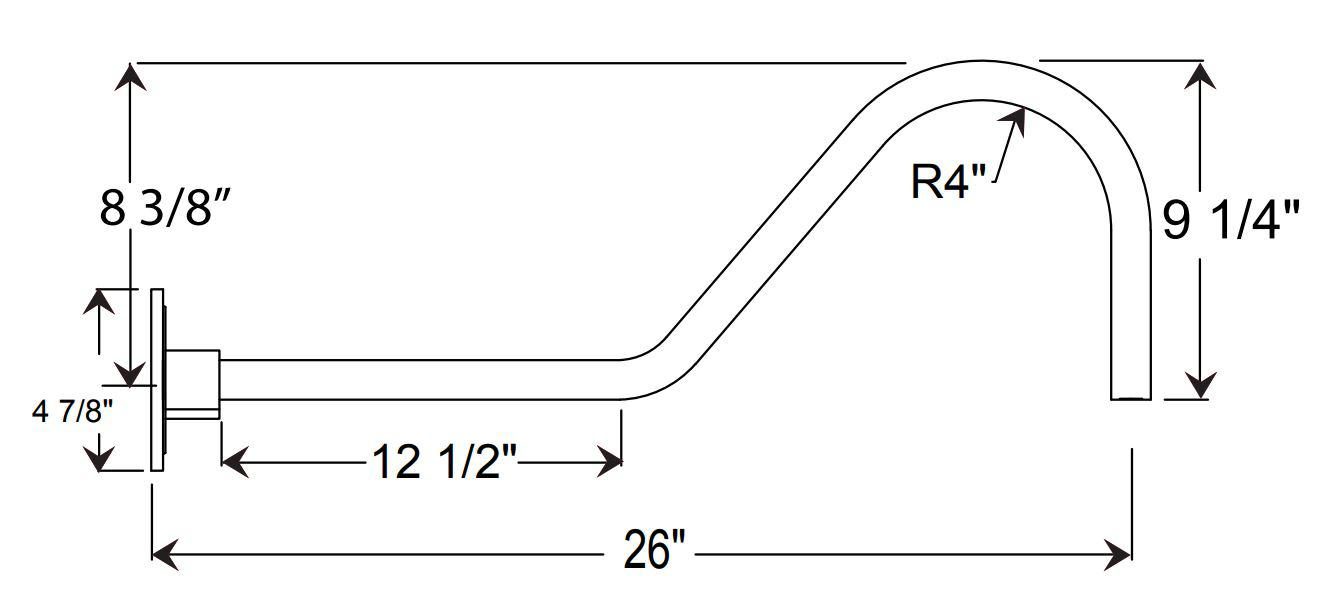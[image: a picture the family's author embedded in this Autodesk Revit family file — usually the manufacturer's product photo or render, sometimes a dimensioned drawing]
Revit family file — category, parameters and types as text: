
# Revit family: OSAC-24,36 MB
name_source: partatom
category: Lighting Fixtures
units: mm (PartAtom-declared; Revit-internal decimal feet)

## family parameters
Always vertical = Yes
Cut with Voids When Loaded = No
Light Source = Yes
OmniClass Number = 23.80.70.00
OmniClass Title = Lighting
Part Type = Normal
Room Calculation Point = No
Round Connector Dimension = Use Diameter
Shared = No
Work Plane-Based = No

## types (2) — shared parameters
Apparent Load = 200 VA
Body Colour = Spun aluminium
Body Material = body
Bulb = Bulb
CRI = >90
Color Filter = 16777215
Construction Material = Heavy Duty spun aluminum.
Default Elevation = 0' - 0"
Description = 120-277 Voltage
Dimming = 1%
Dimming Lamp Color Temperature Shift = <None>
Efficiency = 65-125 lumens per watt
INSIDE BODY = INSIDE BODY
Lamp = MB
Life = L70 50,000 hours
Load Classification = Lighting
Manufacturer = ANP Lighting
Photometric Web File = generic.ies
Power Factor = 1
Tilt Angle = 90.00°
URL = https://www.anplighting.com
Voltage = 277 V
Warranty = 5 year limited warranty
Wattage Comments = 200W Max

## per-type parameters (varying)
| type | Fixture Diameter | Fixture Height | OSAC24 | OSAC36 | Weight |
| OSAC24 | 2' - 0" | 0' - 8" | Yes | No | 6.5 lbs |
| OSAC36 | 3' - 0" | 1' - 0" | No | Yes | 12.0 lbs |

note: column(s) folded — value = type name in every type: Model

## geometry (parser evidence)
native form markers: Sweep x28
no freeform markers — native parametric forms only
